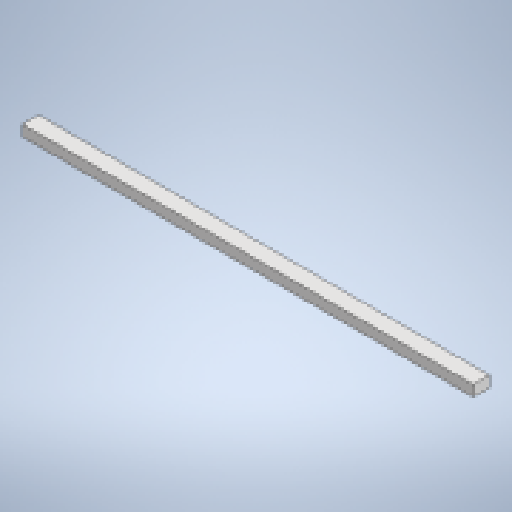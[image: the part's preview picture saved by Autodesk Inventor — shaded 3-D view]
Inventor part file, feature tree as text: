
AUTODESK INVENTOR PART (.ipt)
format: ipt  version: 2025.3 (Build 293356030, 356C)  size: 133,632 bytes
history: native  units: mm
features: extrude x1, sketch x1
ambient origin geometry x8: Origin, YZ Plane, XZ Plane, XY Plane, X Axis, Y Axis, Z Axis, Center Point
bodies: Solid1 (feature_tree)
feature tree (2):
  extrude  "Extrusion1"  Depth=6.0mm
  sketch  "Sketch1"  dims[d0=9.0mm d1=6.0mm d2=250.0mm d3=0.0mm]
